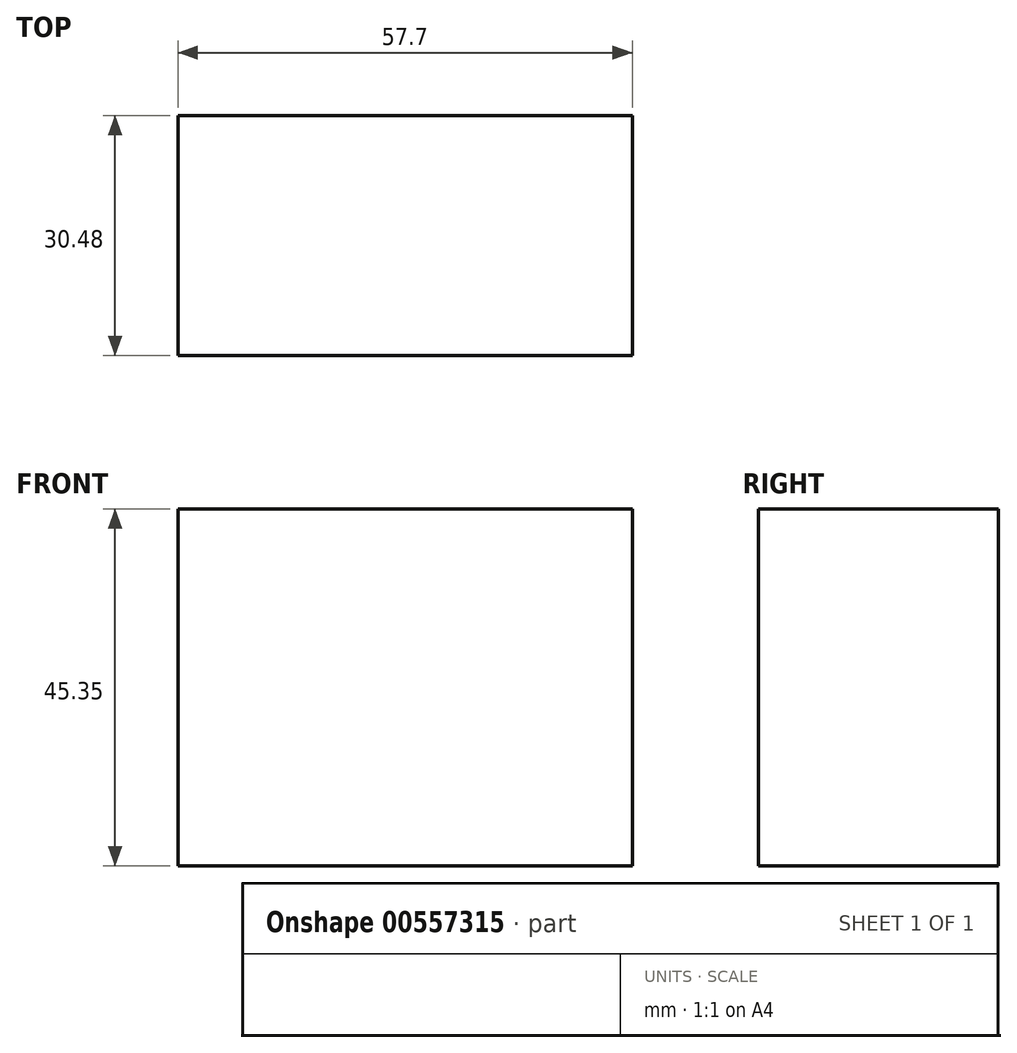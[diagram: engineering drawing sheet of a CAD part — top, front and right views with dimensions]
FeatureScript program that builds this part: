
annotation { "Feature Type Name" : "Feature", "Feature Type Description" : "" }
export const myFeature = defineFeature(function(context is Context, id is Id, definition is map)
    precondition{}
    {
        {
            var Q0;
            Q0=qCreatedBy(makeId("Front.planeOp"),FACE);
            var sketch = newSketch(context, id + "F0", { "sketchPlane" : qUnion([Q0])});
            skLineSegment(sketch, "E0.bottom", {"start": v(11.21, 94.58) * mm, "end": v(-46.5, 94.58) * mm});
            skLineSegment(sketch, "E0.top", {"start": v(11.21, 49.23) * mm, "end": v(-46.5, 49.23) * mm});
            skLineSegment(sketch, "E0.left", {"start": v(11.21, 94.58) * mm, "end": v(11.21, 49.23) * mm});
            skLineSegment(sketch, "E0.right", {"start": v(-46.5, 94.58) * mm, "end": v(-46.5, 49.23) * mm});
            skSolve(sketch);
        }
        {
            var Q0;
            Q0 = qSketchRegion(id + "F0", true);
            extrude(context, id + "F1", {"entities" : qUnion([Q0]), "depth" : 30.48 * mm, "offsetDistance" : 30.48 * mm});
        }
    });
